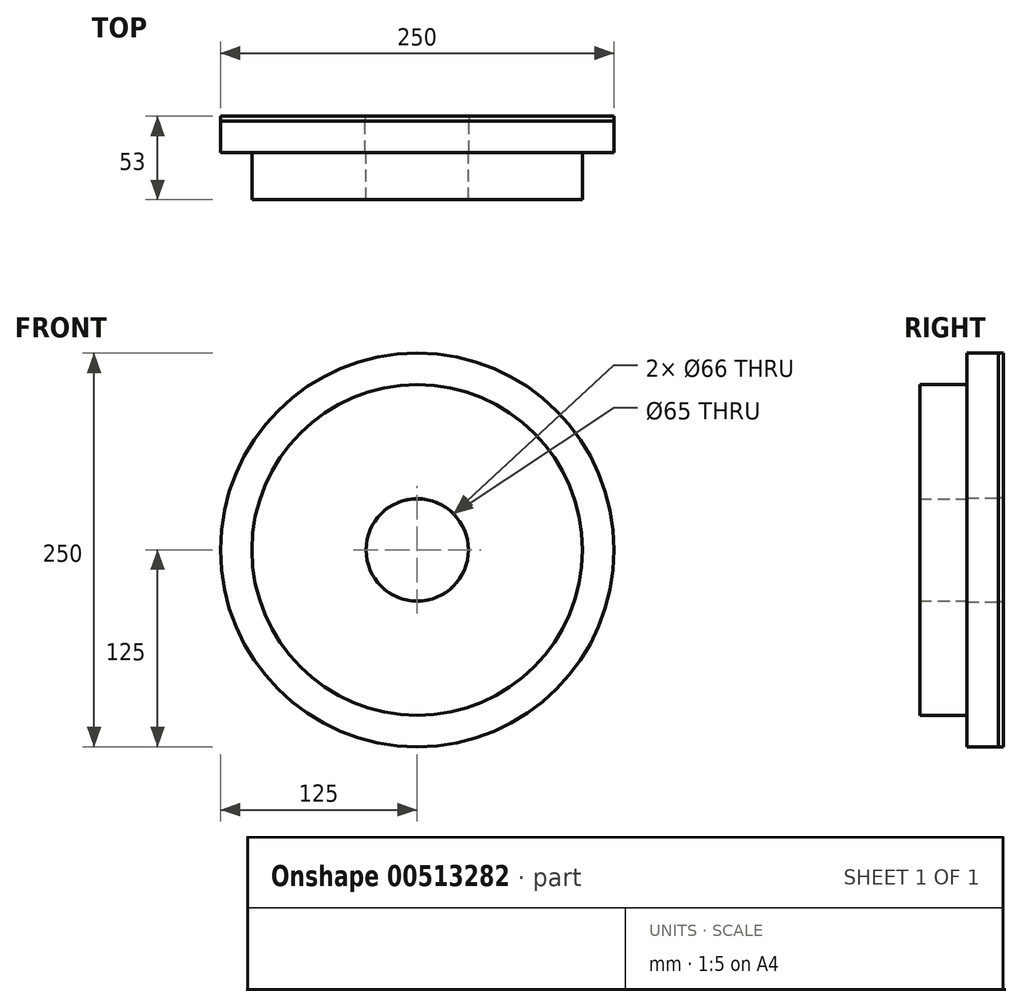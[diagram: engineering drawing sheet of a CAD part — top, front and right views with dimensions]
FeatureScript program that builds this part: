
annotation { "Feature Type Name" : "Feature", "Feature Type Description" : "" }
export const myFeature = defineFeature(function(context is Context, id is Id, definition is map)
    precondition{}
    {
        {
            var Q0;
            Q0=qCreatedBy(makeId("Front.planeOp"),FACE);
            var sketch = newSketch(context, id + "F0", { "sketchPlane" : qUnion([Q0])});
            skCircle(sketch, "E0", {"center": v(0, 0) * mm, "radius": 32.5 * mm});
            skCircle(sketch, "E1", {"center": v(0, 0) * mm, "radius": 105 * mm});
            skSolve(sketch);
        }
        {
            var Q0;
            Q0=makeQuery(id+"F0.imprint","IMPRINT",FACE,{"disambiguationData":[TD([[makeQuery(id+"F0.imprint","IMPRINT",EDGE,{"derivedFrom":sQuery(id+"F0.wireOp",EDGE,"E0")}),-1.0]])]});
            extrude(context, id + "F1", {"entities" : qUnion([Q0]), "depth" : 30 * mm});
        }
        {
            var Q0;
            Q0=makeQuery(id+"F1.opExtrude","CAP_FACE",FACE,{"disambiguationData":[OSD([sQuery(id+"F0.wireOp",EDGE,"E0"),sQuery(id+"F0.wireOp",EDGE,"E1")])],"isStart":true});
            cPlane(context, id + "F2", {"entities" : qUnion([Q0]), "cplaneType" : CPlaneType.OFFSET, "offset" : 20 * mm, "width" : 150 * mm, "height" : 150 * mm});
        }
        {
            var Q0;
            Q0=qCreatedBy(id+"F2.planeOp",FACE);
            var sketch = newSketch(context, id + "F3", { "sketchPlane" : qUnion([Q0])});
            skCircle(sketch, "E2", {"center": v(0, 0) * mm, "radius": 110 * mm, "construction": true});
            skCircle(sketch, "E3", {"center": v(0, 0) * mm, "radius": 33 * mm});
            skCircle(sketch, "E4", {"center": v(0, 0) * mm, "radius": 125 * mm});
            skSolve(sketch);
        }
        {
            var Q0;
            Q0=makeQuery(id+"F3.imprint","IMPRINT",FACE,{"disambiguationData":[TD([[makeQuery(id+"F3.imprint","IMPRINT",EDGE,{"derivedFrom":sQuery(id+"F3.wireOp",EDGE,"E3")}),-1.0]])]});
            extrude(context, id + "F4", {"entities" : qUnion([Q0]), "oppositeDirection" : true, "depth" : 20 * mm});
        }
        {
            var Q0;
            Q0=makeQuery(id+"F3.imprint","IMPRINT",FACE,{"disambiguationData":[TD([[makeQuery(id+"F3.imprint","IMPRINT",EDGE,{"derivedFrom":sQuery(id+"F3.wireOp",EDGE,"E3")}),-1.0]])]});
            extrude(context, id + "F5", {"entities" : qUnion([Q0]), "depth" : 3 * mm});
        }
    });
